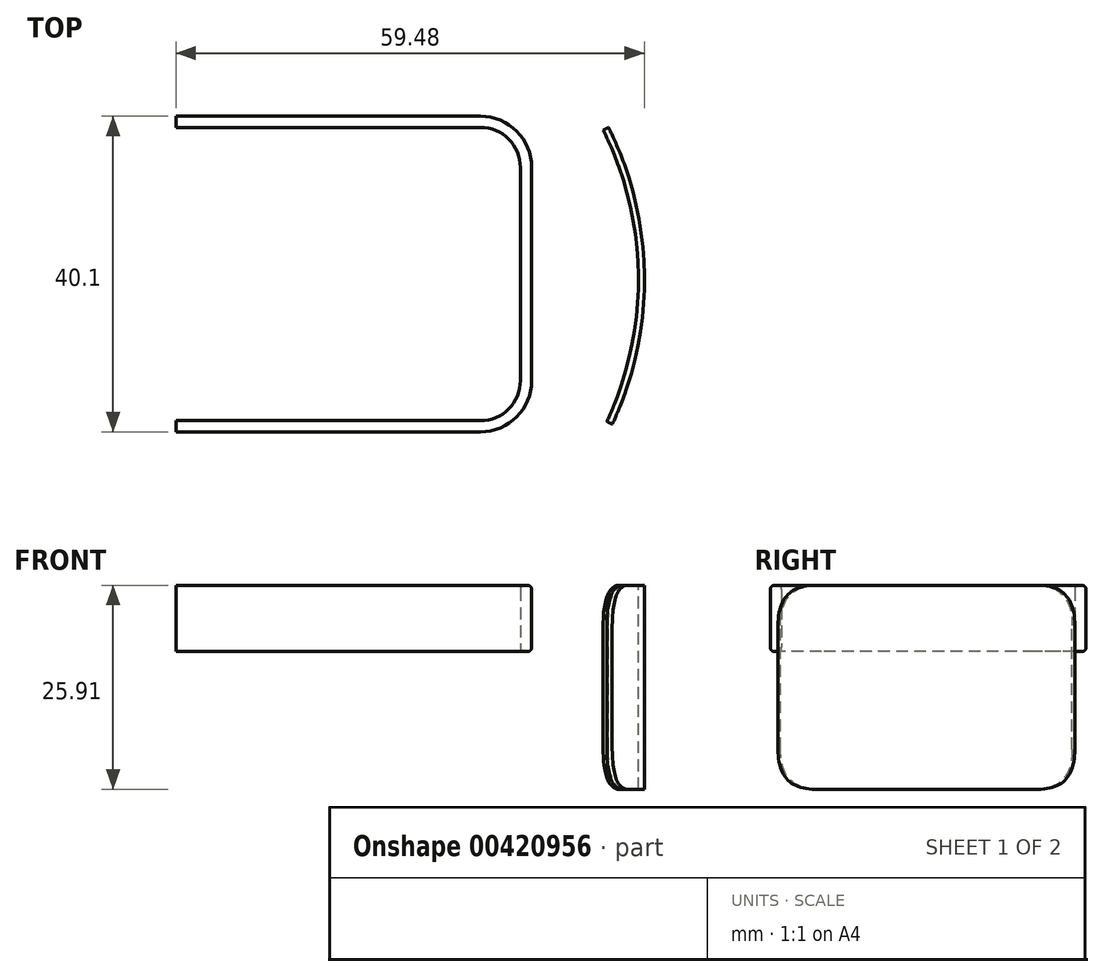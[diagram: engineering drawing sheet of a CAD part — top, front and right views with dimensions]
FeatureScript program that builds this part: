
annotation { "Feature Type Name" : "Feature", "Feature Type Description" : "" }
export const myFeature = defineFeature(function(context is Context, id is Id, definition is map)
    precondition{}
    {
        {
            var Q0;
            Q0=qCreatedBy(makeId("Top.planeOp"),FACE);
            var sketch = newSketch(context, id + "F0", { "sketchPlane" : qUnion([Q0])});
            skLineSegment(sketch, "E0", {"start": v(0, 0) * mm, "end": v(38.65, 0) * mm});
            skLineSegment(sketch, "E1", {"start": v(43.73, -5.08) * mm, "end": v(43.73, -32.16) * mm});
            skLineSegment(sketch, "E2", {"start": v(38.65, -37.24) * mm, "end": v(0, -37.24) * mm});
            skPoint(sketch, "E3.visualSharp", {"position": v(43.73, 0) * mm});
            skArc(sketch, "E3.filletArc", {"start": v(43.73, -5.08) * mm, "mid": v(42.24, -1.49) * mm, "end": v(38.65, 0) * mm});
            skPoint(sketch, "E4.visualSharp", {"position": v(43.73, -37.24) * mm});
            skArc(sketch, "E4.filletArc", {"start": v(38.65, -37.24) * mm, "mid": v(42.24, -35.76) * mm, "end": v(43.73, -32.16) * mm});
            skSolve(sketch);
        }
        {
            var Q0;
            Q0=qCreatedBy(makeId("Right.planeOp"),FACE);
            var sketch = newSketch(context, id + "F1", { "sketchPlane" : qUnion([Q0])});
            skLineSegment(sketch, "E5.bottom", {"start": v(0.5, 0) * mm, "end": v(0.92, 0) * mm});
            skLineSegment(sketch, "E5.top", {"start": v(0.5, -8.4) * mm, "end": v(0.92, -8.4) * mm});
            skLineSegment(sketch, "E5.left", {"start": v(0, -0.5) * mm, "end": v(0, -7.9) * mm});
            skLineSegment(sketch, "E5.right", {"start": v(1.43, -0.5) * mm, "end": v(1.43, -7.9) * mm});
            skPoint(sketch, "E6.visualSharp", {"position": v(1.43, -8.4) * mm});
            skArc(sketch, "E6.filletArc", {"start": v(0.92, -8.4) * mm, "mid": v(1.28, -8.26) * mm, "end": v(1.43, -7.9) * mm});
            skPoint(sketch, "E7.visualSharp", {"position": v(0, -8.4) * mm});
            skArc(sketch, "E7.filletArc", {"start": v(0, -7.9) * mm, "mid": v(0.15, -8.26) * mm, "end": v(0.5, -8.4) * mm});
            skPoint(sketch, "E8.visualSharp", {"position": v(1.43, 0) * mm});
            skArc(sketch, "E8.filletArc", {"start": v(1.43, -0.5) * mm, "mid": v(1.28, -0.15) * mm, "end": v(0.92, 0) * mm});
            skPoint(sketch, "E9.visualSharp", {"position": v(0, 0) * mm});
            skArc(sketch, "E9.filletArc", {"start": v(0.5, 0) * mm, "mid": v(0.15, -0.15) * mm, "end": v(0, -0.5) * mm});
            skSolve(sketch);
        }
        {
            var Q0;
            Q0=makeQuery(id+"F1.imprint","IMPRINT",FACE,{"disambiguationData":[TD([[makeQuery(id+"F1.imprint","IMPRINT",EDGE,{"derivedFrom":sQuery(id+"F1.wireOp",EDGE,"E5.bottom")}),-1.0]])]});
            var Q1;
            Q1=sQuery(id+"F0.wireOp",EDGE,"E0");
            var Q2;
            Q2=sQuery(id+"F0.wireOp",EDGE,"E3.filletArc");
            var Q3;
            Q3=sQuery(id+"F0.wireOp",EDGE,"E1");
            var Q4;
            Q4=sQuery(id+"F0.wireOp",EDGE,"E4.filletArc");
            var Q5;
            Q5=sQuery(id+"F0.wireOp",EDGE,"E2");
            sweep(context, id + "F2", {"profiles" : qUnion([Q0]), "path" : qUnion([Q1, Q2, Q3, Q4, Q5])});
        }
        {
            var Q0;
            Q0=qCreatedBy(makeId("Top.planeOp"),FACE);
            var sketch = newSketch(context, id + "F3", { "sketchPlane" : qUnion([Q0])});
            skArc(sketch, "E10", {"start": v(55.4, -37.7) * mm, "mid": v(59.48, -18.8) * mm, "end": v(54.92, 0) * mm});
            skArc(sketch, "E11.0", {"start": v(54.7, -37.37) * mm, "mid": v(58.72, -18.8) * mm, "end": v(54.24, -0.34) * mm});
            skLineSegment(sketch, "E12", {"start": v(54.92, 0) * mm, "end": v(54.24, -0.34) * mm});
            skLineSegment(sketch, "E13", {"start": v(55.4, -37.7) * mm, "end": v(54.7, -37.37) * mm});
            skSolve(sketch);
        }
        {
            var Q0;
            Q0=makeQuery(id+"F3.imprint","IMPRINT",FACE,{"disambiguationData":[TD([[makeQuery(id+"F3.imprint","IMPRINT",EDGE,{"derivedFrom":sQuery(id+"F3.wireOp",EDGE,"E10")}),1.0]])]});
            extrude(context, id + "F4", {"entities" : qUnion([Q0]), "oppositeDirection" : true, "depth" : 25.9 * mm});
        }
        {
            var Q0;
            Q0=makeQuery(id+"F4.opExtrude","CAP_EDGE",EDGE,{"disambiguationData":[OSD([sQuery(id+"F3.wireOp",EDGE,"E13")])],"isStart":false});
            var Q1;
            Q1=makeQuery(id+"F4.opExtrude","CAP_EDGE",EDGE,{"disambiguationData":[OSD([sQuery(id+"F3.wireOp",EDGE,"E12")])],"isStart":false});
            var Q2;
            Q2=makeQuery(id+"F4.opExtrude","CAP_EDGE",EDGE,{"disambiguationData":[OSD([sQuery(id+"F3.wireOp",EDGE,"E13")])],"isStart":true});
            var Q3;
            Q3=makeQuery(id+"F4.opExtrude","CAP_EDGE",EDGE,{"disambiguationData":[OSD([sQuery(id+"F3.wireOp",EDGE,"E12")])],"isStart":true});
            fillet(context, id + "F5", {"entities" : qUnion([Q0, Q1, Q2, Q3]), "radius" : 5.08 * mm, "rho" : 0.5, "crossSection" : FilletCrossSection.CONIC, "allowEdgeOverflow" : false});
        }
    });
